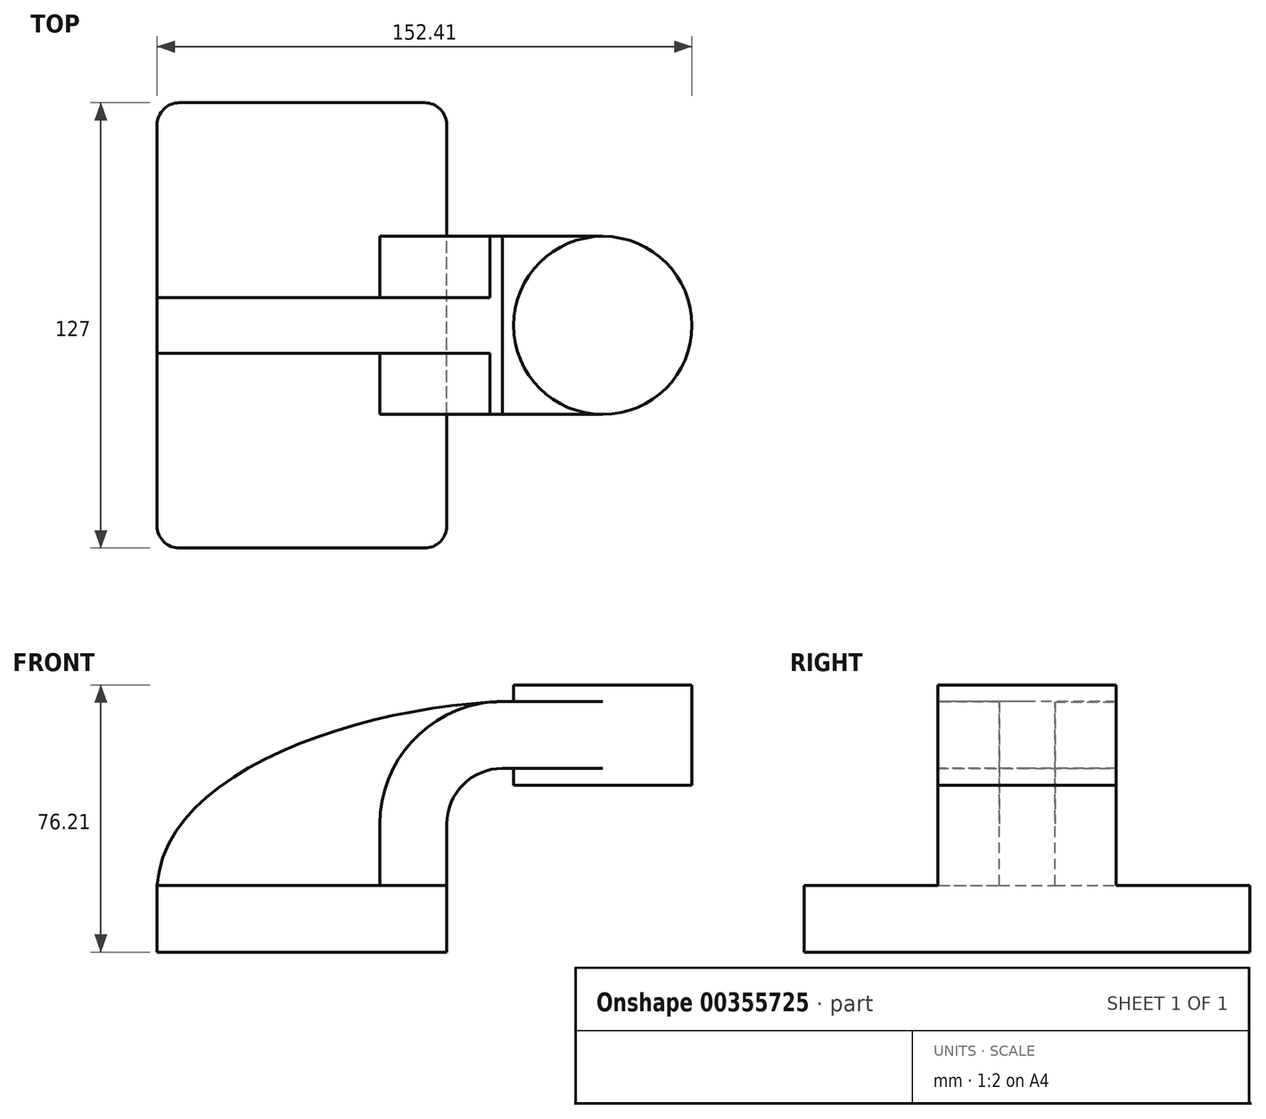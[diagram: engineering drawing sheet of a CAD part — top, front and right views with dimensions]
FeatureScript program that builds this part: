
annotation { "Feature Type Name" : "Feature", "Feature Type Description" : "" }
export const myFeature = defineFeature(function(context is Context, id is Id, definition is map)
    precondition{}
    {
        {
            var Q0;
            Q0=qCreatedBy(makeId("Front.planeOp"),FACE);
            var sketch = newSketch(context, id + "F0", { "sketchPlane" : qUnion([Q0])});
            skLineSegment(sketch, "E0.bottom", {"start": v(-41.28, -9.53) * mm, "end": v(41.28, -9.53) * mm});
            skLineSegment(sketch, "E0.top", {"start": v(-41.28, 9.52) * mm, "end": v(41.28, 9.52) * mm});
            skLineSegment(sketch, "E0.left", {"start": v(-41.27, -9.53) * mm, "end": v(-41.28, 9.52) * mm});
            skLineSegment(sketch, "E0.right", {"start": v(41.28, -9.53) * mm, "end": v(41.28, 9.52) * mm});
            skPoint(sketch, "E0.middle", {"position": v(0, 0) * mm});
            skLineSegment(sketch, "E1.bottom", {"start": v(111.12, 66.68) * mm, "end": v(60.32, 66.68) * mm});
            skLineSegment(sketch, "E1.top", {"start": v(111.13, 38.1) * mm, "end": v(60.32, 38.1) * mm});
            skLineSegment(sketch, "E1.left", {"start": v(111.13, 66.68) * mm, "end": v(111.13, 38.1) * mm});
            skLineSegment(sketch, "E1.right", {"start": v(60.32, 66.68) * mm, "end": v(60.32, 38.1) * mm});
            skPoint(sketch, "E1.middle", {"position": v(85.73, 52.39) * mm});
            skLineSegment(sketch, "E2", {"start": v(41.27, 9.52) * mm, "end": v(41.27, 27) * mm});
            skArc(sketch, "E3", {"start": v(41.28, 27) * mm, "mid": v(45.92, 38.23) * mm, "end": v(57.15, 42.88) * mm});
            skLineSegment(sketch, "E4", {"start": v(57.15, 42.88) * mm, "end": v(85.72, 42.88) * mm});
            skLineSegment(sketch, "E5.0", {"start": v(57.15, 61.93) * mm, "end": v(85.72, 61.93) * mm});
            skArc(sketch, "E5.1", {"start": v(22.23, 27) * mm, "mid": v(32.45, 51.7) * mm, "end": v(57.15, 61.93) * mm});
            skLineSegment(sketch, "E5.2", {"start": v(22.22, 9.52) * mm, "end": v(22.22, 27) * mm});
            skLineSegment(sketch, "E6", {"start": v(85.72, 38.1) * mm, "end": v(85.72, 66.68) * mm});
            skFitSpline(sketch, "E7", {"points": [v(-41.28, 9.52) * mm, v(57.15, 61.93) * mm], "startDerivative": vector(6.73, 98.07) * mm, "endDerivative": vector(123.73, 4.93) * mm});
            skSolve(sketch);
        }
        {
            var Q0;
            Q0=makeQuery(id+"F0.imprint","IMPRINT",FACE,{"disambiguationData":[TD([[makeQuery(id+"F0.imprint","IMPRINT",EDGE,{"derivedFrom":sQuery(id+"F0.wireOp",EDGE,"E0.bottom")}),1.0]])]});
            extrude(context, id + "F1", {"entities" : qUnion([Q0]), "endBound" : BoundingType.SYMMETRIC, "depth" : 127 * mm});
        }
        {
            var Q0;
            {var subQ1=sQuery(id+"F0.wireOp",EDGE,"E2");Q0=makeQuery(id+"F0.imprint","IMPRINT",FACE,{"disambiguationData":[TD([[makeQuery(id+"F0.imprint","IMPRINT",EDGE,{"derivedFrom":subQ1}),1.0]])]});}
            extrude(context, id + "F2", {"entities" : qUnion([Q0]), "operationType" : NewBodyOperationType.ADD, "endBound" : BoundingType.SYMMETRIC, "depth" : 50.8 * mm});
        }
        {
            var Q0;
            {var subQ0=sQuery(id+"F0.wireOp",EDGE,"E5.0");var subQ1=sQuery(id+"F0.wireOp",EDGE,"E1.right");var subQ2=makeQuery(id+"F0.imprint","INTERSECT",VERTEX,{"derivedFrom":[subQ1,subQ0]});Q0=makeQuery(id+"F0.imprint","IMPRINT",FACE,{"disambiguationData":[TD([[makeQuery(id+"F0.imprint","IMPRINT",EDGE,{"disambiguationData":[TD([[subQ2,-1.0]])],"derivedFrom":subQ1}),1.0]])]});}
            extrude(context, id + "F3", {"entities" : qUnion([Q0]), "operationType" : NewBodyOperationType.ADD, "endBound" : BoundingType.SYMMETRIC, "depth" : 50.8 * mm});
        }
        {
            var Q0;
            {var subQ3=sQuery(id+"F0.wireOp",EDGE,"E5.2");Q0=makeQuery(id+"F0.imprint","IMPRINT",FACE,{"disambiguationData":[TD([[makeQuery(id+"F0.imprint","IMPRINT",EDGE,{"derivedFrom":subQ3}),1.0]])]});}
            extrude(context, id + "F4", {"entities" : qUnion([Q0]), "operationType" : NewBodyOperationType.ADD, "endBound" : BoundingType.SYMMETRIC, "depth" : 15.88 * mm});
        }
        {
            var Q0;
            {var subQ0=sQuery(id+"F0.wireOp",EDGE,"E1.left");Q0=makeQuery(id+"F0.imprint","IMPRINT",FACE,{"disambiguationData":[TD([[makeQuery(id+"F0.imprint","IMPRINT",EDGE,{"derivedFrom":subQ0}),-1.0]])]});}
            var Q1;
            Q1=sQuery(id+"F0.wireOp",EDGE,"E6");
            revolve(context, id + "F5", {"operationType" : NewBodyOperationType.ADD, "entities" : qUnion([Q0]), "axis" : qUnion([Q1]), "revolveType" : RevolveType.FULL});
        }
        {
            var Q0;
            Q0=makeQuery(id+"F1.opExtrude","CAP_EDGE",EDGE,{"disambiguationData":[OSD([sQuery(id+"F0.wireOp",EDGE,"E0.right")])],"isStart":false});
            var Q1;
            Q1=makeQuery(id+"F1.opExtrude","CAP_EDGE",EDGE,{"disambiguationData":[OSD([sQuery(id+"F0.wireOp",EDGE,"E0.right")])],"isStart":true});
            var Q2;
            Q2=makeQuery(id+"F1.opExtrude","CAP_EDGE",EDGE,{"disambiguationData":[OSD([sQuery(id+"F0.wireOp",EDGE,"E0.left")])],"isStart":false});
            var Q3;
            Q3=makeQuery(id+"F1.opExtrude","CAP_EDGE",EDGE,{"disambiguationData":[OSD([sQuery(id+"F0.wireOp",EDGE,"E0.left")])],"isStart":true});
            fillet(context, id + "F6", {"entities" : qUnion([Q0, Q1, Q2, Q3]), "radius" : 6.35 * mm, "tangentPropagation" : true, "allowEdgeOverflow" : false});
        }
    });
